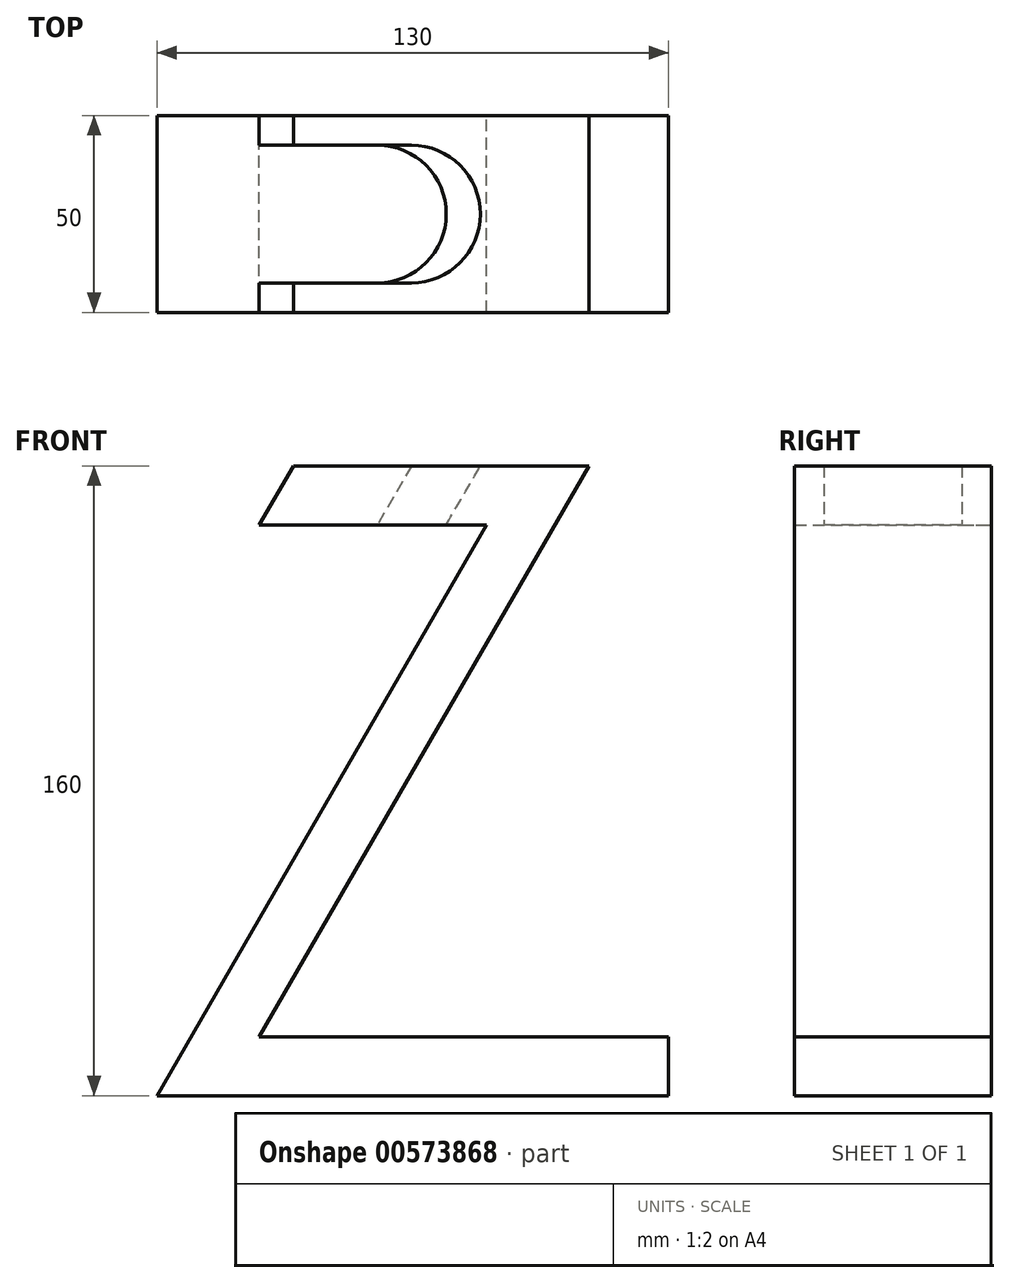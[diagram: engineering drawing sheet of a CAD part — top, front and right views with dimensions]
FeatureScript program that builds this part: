
annotation { "Feature Type Name" : "Feature", "Feature Type Description" : "" }
export const myFeature = defineFeature(function(context is Context, id is Id, definition is map)
    precondition{}
    {
        {
            var Q0;
            Q0=qCreatedBy(makeId("Front.planeOp"),FACE);
            var sketch = newSketch(context, id + "F0", { "sketchPlane" : qUnion([Q0])});
            skLineSegment(sketch, "E0", {"start": v(0, 0) * mm, "end": v(83.72, 145) * mm});
            skLineSegment(sketch, "E1", {"start": v(83.72, 145) * mm, "end": v(25.98, 145) * mm});
            skLineSegment(sketch, "E2", {"start": v(25.98, 145) * mm, "end": v(34.64, 160) * mm});
            skLineSegment(sketch, "E3", {"start": v(34.64, 160) * mm, "end": v(109.7, 160) * mm});
            skLineSegment(sketch, "E4", {"start": v(109.7, 160) * mm, "end": v(25.98, 15) * mm});
            skLineSegment(sketch, "E5", {"start": v(25.98, 15) * mm, "end": v(130, 15) * mm});
            skLineSegment(sketch, "E6", {"start": v(130, 15) * mm, "end": v(130, 0) * mm});
            skLineSegment(sketch, "E7", {"start": v(130, 0) * mm, "end": v(0, 0) * mm});
            skSolve(sketch);
        }
        {
            var Q0;
            Q0=makeQuery(id+"F0.imprint","IMPRINT",FACE,{"disambiguationData":[TD([[makeQuery(id+"F0.imprint","IMPRINT",EDGE,{"derivedFrom":sQuery(id+"F0.wireOp",EDGE,"E0")}),-1.0]])]});
            extrude(context, id + "F1", {"entities" : qUnion([Q0]), "depth" : 50 * mm, "offsetDistance" : 25 * mm});
        }
        {
            var Q0;
            Q0=makeQuery(id+"F1.opExtrude","SWEPT_FACE",FACE,{"disambiguationData":[OSD([sQuery(id+"F0.wireOp",EDGE,"E3")])]});
            var sketch = newSketch(context, id + "F2", { "sketchPlane" : qUnion([Q0])});
            skArc(sketch, "E8", {"start": v(64.64, -42.5) * mm, "mid": v(82.14, -25) * mm, "end": v(64.64, -7.5) * mm});
            skPoint(sketch, "E8.centerSnap0", {"position": v(34.64, -25) * mm});
            skLineSegment(sketch, "E9", {"start": v(64.64, -7.5) * mm, "end": v(34.64, -7.5) * mm});
            skLineSegment(sketch, "E10", {"start": v(64.64, -42.5) * mm, "end": v(34.64, -42.5) * mm});
            skLineSegment(sketch, "E11", {"start": v(34.64, -42.5) * mm, "end": v(34.64, -7.5) * mm});
            skSolve(sketch);
        }
        {
            var Q0;
            Q0=makeQuery(id+"F1.opExtrude","SWEPT_FACE",FACE,{"disambiguationData":[OSD([sQuery(id+"F0.wireOp",EDGE,"E1")])]});
            var sketch = newSketch(context, id + "F3", { "sketchPlane" : qUnion([Q0])});
            skArc(sketch, "E12", {"start": v(55.98, 7.5) * mm, "mid": v(73.48, 25) * mm, "end": v(55.98, 42.5) * mm});
            skPoint(sketch, "E12.centerSnap0", {"position": v(25.98, 25) * mm});
            skLineSegment(sketch, "E13", {"start": v(55.98, 42.5) * mm, "end": v(25.98, 42.5) * mm});
            skLineSegment(sketch, "E14", {"start": v(55.98, 7.5) * mm, "end": v(25.98, 7.5) * mm});
            skLineSegment(sketch, "E15", {"start": v(25.98, 7.5) * mm, "end": v(25.98, 42.5) * mm});
            skSolve(sketch);
        }
        {
            var Q1;
            Q1=makeQuery(id+"F2.imprint","IMPRINT",FACE,{"disambiguationData":[TD([[makeQuery(id+"F2.imprint","IMPRINT",EDGE,{"derivedFrom":sQuery(id+"F2.wireOp",EDGE,"E8")}),1.0]])]});
            var Q2;
            Q2=makeQuery(id+"F3.imprint","IMPRINT",FACE,{"disambiguationData":[TD([[makeQuery(id+"F3.imprint","IMPRINT",EDGE,{"derivedFrom":sQuery(id+"F3.wireOp",EDGE,"E12")}),1.0]])]});
            loft(context, id + "F4", {"operationType" : NewBodyOperationType.REMOVE, "sheetProfilesArray" : [{ "sheetProfileEntities" : qUnion([Q1]) }, { "sheetProfileEntities" : qUnion([Q2]) }]});
        }
    });
